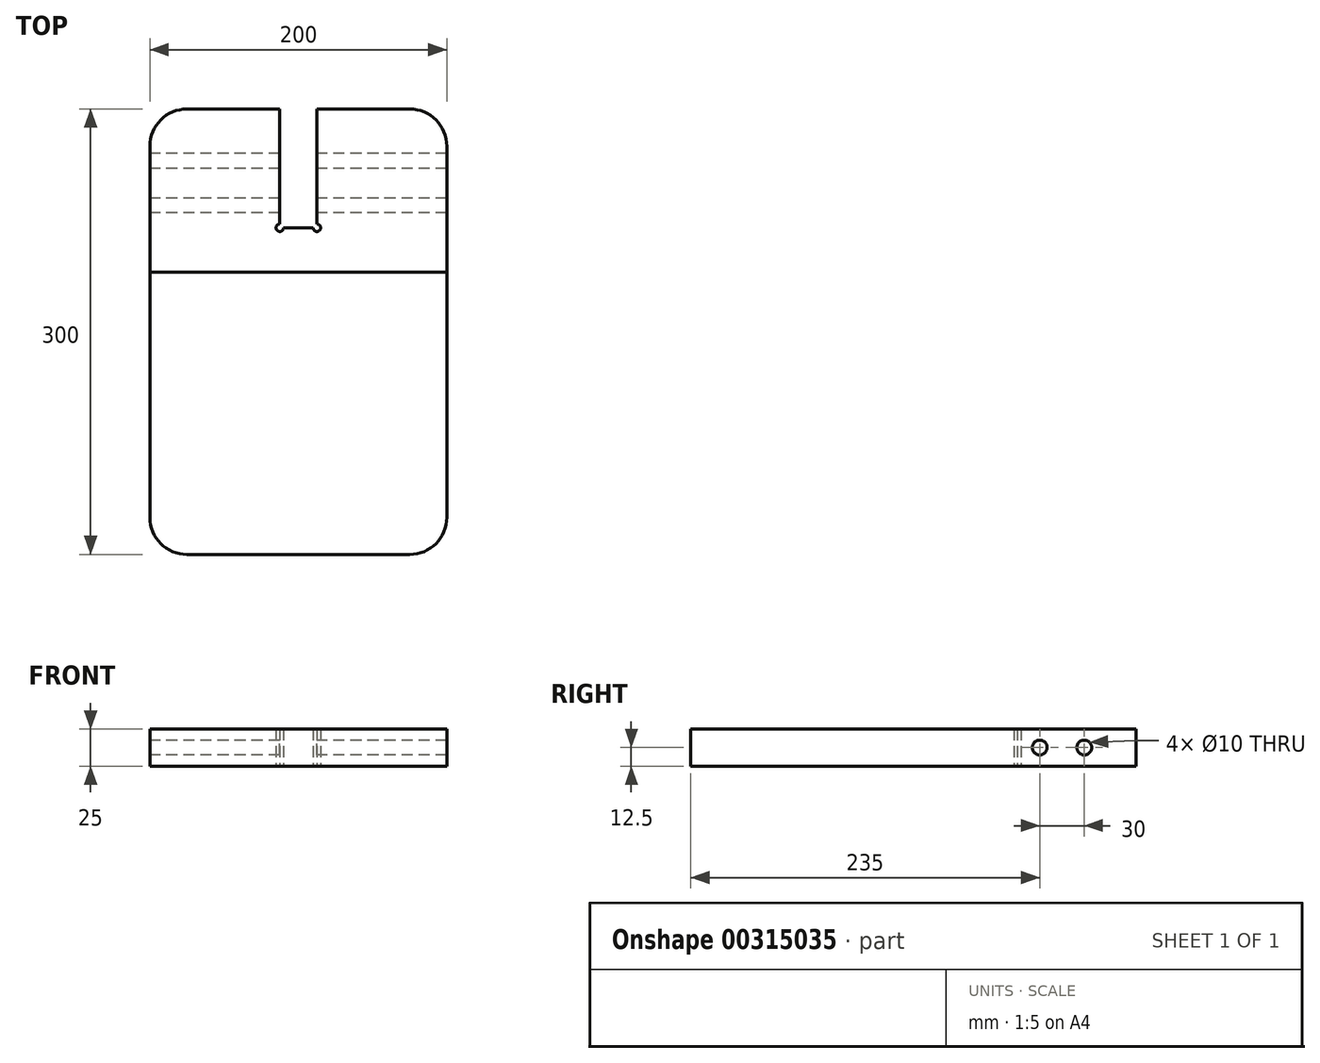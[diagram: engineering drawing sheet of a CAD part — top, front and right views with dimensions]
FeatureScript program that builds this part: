
annotation { "Feature Type Name" : "Feature", "Feature Type Description" : "" }
export const myFeature = defineFeature(function(context is Context, id is Id, definition is map)
    precondition{}
    {
        {
            var Q0;
            Q0=qCreatedBy(makeId("Top.planeOp"),FACE);
            var sketch = newSketch(context, id + "F0", { "sketchPlane" : qUnion([Q0])});
            skLineSegment(sketch, "E0.bottom", {"start": v(-75, 150) * mm, "end": v(-12.5, 150) * mm});
            skLineSegment(sketch, "E0.top", {"start": v(-75, -150) * mm, "end": v(75, -150) * mm});
            skLineSegment(sketch, "E0.left", {"start": v(-100, 125) * mm, "end": v(-100, -125) * mm});
            skLineSegment(sketch, "E0.right", {"start": v(100, 125) * mm, "end": v(100, -125) * mm});
            skPoint(sketch, "E0.middle", {"position": v(0, 0) * mm});
            skLineSegment(sketch, "E1.top", {"start": v(10, 70) * mm, "end": v(-10, 70) * mm});
            skLineSegment(sketch, "E1.left", {"start": v(12.5, 150) * mm, "end": v(12.5, 72.5) * mm});
            skLineSegment(sketch, "E1.right", {"start": v(-12.5, 150) * mm, "end": v(-12.5, 72.5) * mm});
            skPoint(sketch, "E1.middle", {"position": v(0, 150) * mm});
            skArc(sketch, "E2", {"start": v(-12.5, 72.5) * mm, "mid": v(-14.27, 68.23) * mm, "end": v(-10, 70) * mm});
            skArc(sketch, "E3", {"start": v(10, 70) * mm, "mid": v(14.27, 68.23) * mm, "end": v(12.5, 72.5) * mm});
            skLineSegment(sketch, "E4.trimOffspring", {"start": v(12.5, 150) * mm, "end": v(75, 150) * mm});
            skPoint(sketch, "E5.orphan", {"position": v(-12.5, 230) * mm});
            skPoint(sketch, "E6.orphan", {"position": v(12.5, 230) * mm});
            skPoint(sketch, "E7.visualSharp", {"position": v(-100, 150) * mm});
            skArc(sketch, "E7.filletArc", {"start": v(-75, 150) * mm, "mid": v(-92.68, 142.68) * mm, "end": v(-100, 125) * mm});
            skPoint(sketch, "E8.visualSharp", {"position": v(100, 150) * mm});
            skArc(sketch, "E8.filletArc", {"start": v(100, 125) * mm, "mid": v(92.68, 142.68) * mm, "end": v(75, 150) * mm});
            skPoint(sketch, "E9.visualSharp", {"position": v(-100, -150) * mm});
            skArc(sketch, "E9.filletArc", {"start": v(-100, -125) * mm, "mid": v(-92.68, -142.68) * mm, "end": v(-75, -150) * mm});
            skPoint(sketch, "E10.visualSharp", {"position": v(100, -150) * mm});
            skArc(sketch, "E10.filletArc", {"start": v(75, -150) * mm, "mid": v(92.68, -142.68) * mm, "end": v(100, -125) * mm});
            skSolve(sketch);
        }
        {
            var Q0;
            Q0=makeQuery(id+"F0.imprint","IMPRINT",FACE,{"disambiguationData":[TD([[makeQuery(id+"F0.imprint","IMPRINT",EDGE,{"derivedFrom":sQuery(id+"F0.wireOp",EDGE,"E0.bottom")}),-1.0]])]});
            extrude(context, id + "F1", {"entities" : qUnion([Q0]), "depth" : 25 * mm});
        }
        {
            var Q0;
            Q0=makeQuery(id+"F1.opExtrude","SWEPT_FACE",FACE,{"disambiguationData":[OSD([sQuery(id+"F0.wireOp",EDGE,"E0.left")])]});
            var sketch = newSketch(context, id + "F2", { "sketchPlane" : qUnion([Q0])});
            skCircle(sketch, "E11", {"center": v(-115, 12.5) * mm, "radius": 5 * mm});
            skPoint(sketch, "E11.centerSnap0", {"position": v(-125, 12.5) * mm});
            skCircle(sketch, "E12", {"center": v(-85, 12.5) * mm, "radius": 5 * mm});
            skSolve(sketch);
        }
        {
            var Q0;
            Q0=makeQuery(id+"F2.imprint","IMPRINT",FACE,{"disambiguationData":[TD([[makeQuery(id+"F2.imprint","IMPRINT",EDGE,{"derivedFrom":sQuery(id+"F2.wireOp",EDGE,"E11")}),1.0]])]});
            var Q1;
            Q1=makeQuery(id+"F2.imprint","IMPRINT",FACE,{"disambiguationData":[TD([[makeQuery(id+"F2.imprint","IMPRINT",EDGE,{"derivedFrom":sQuery(id+"F2.wireOp",EDGE,"E12")}),1.0]])]});
            extrude(context, id + "F3", {"entities" : qUnion([Q0, Q1]), "operationType" : NewBodyOperationType.REMOVE, "endBound" : BoundingType.THROUGH_ALL, "oppositeDirection" : true, "depth" : 25 * mm});
        }
        {
            var Q0;
            Q0=makeQuery(id+"F1.opExtrude","CAP_FACE",FACE,{"disambiguationData":[OSD([sQuery(id+"F0.wireOp",EDGE,"E0.bottom"),sQuery(id+"F0.wireOp",EDGE,"E0.top"),sQuery(id+"F0.wireOp",EDGE,"E0.left"),sQuery(id+"F0.wireOp",EDGE,"E0.right"),sQuery(id+"F0.wireOp",EDGE,"E1.top"),sQuery(id+"F0.wireOp",EDGE,"E1.left"),sQuery(id+"F0.wireOp",EDGE,"E1.right"),sQuery(id+"F0.wireOp",EDGE,"E2"),sQuery(id+"F0.wireOp",EDGE,"E3"),sQuery(id+"F0.wireOp",EDGE,"E4.trimOffspring"),sQuery(id+"F0.wireOp",EDGE,"E7.filletArc"),sQuery(id+"F0.wireOp",EDGE,"E8.filletArc"),sQuery(id+"F0.wireOp",EDGE,"E9.filletArc"),sQuery(id+"F0.wireOp",EDGE,"E10.filletArc")])],"isStart":false});
            var sketch = newSketch(context, id + "F4", { "sketchPlane" : qUnion([Q0])});
            skLineSegment(sketch, "E13.bottom", {"start": v(-100, -150) * mm, "end": v(100, -150) * mm});
            skLineSegment(sketch, "E13.top", {"start": v(-100, 40) * mm, "end": v(100, 40) * mm});
            skLineSegment(sketch, "E13.left", {"start": v(-100, -150) * mm, "end": v(-100, 40) * mm});
            skLineSegment(sketch, "E13.right", {"start": v(100, -150) * mm, "end": v(100, 40) * mm});
            skSolve(sketch);
        }
        {
            var Q0;
            {var subQ2=sQuery(id+"F4.wireOp",EDGE,"E13.top");Q0=makeQuery(id+"F4.imprint","IMPRINT",FACE,{"disambiguationData":[TD([[makeQuery(id+"F4.imprint","IMPRINT",EDGE,{"derivedFrom":subQ2}),-1.0]])]});}
            extrude(context, id + "F5", {"entities" : qUnion([Q0]), "operationType" : NewBodyOperationType.REMOVE, "oppositeDirection" : true, "depth" : 0.01 * mm});
        }
    });
